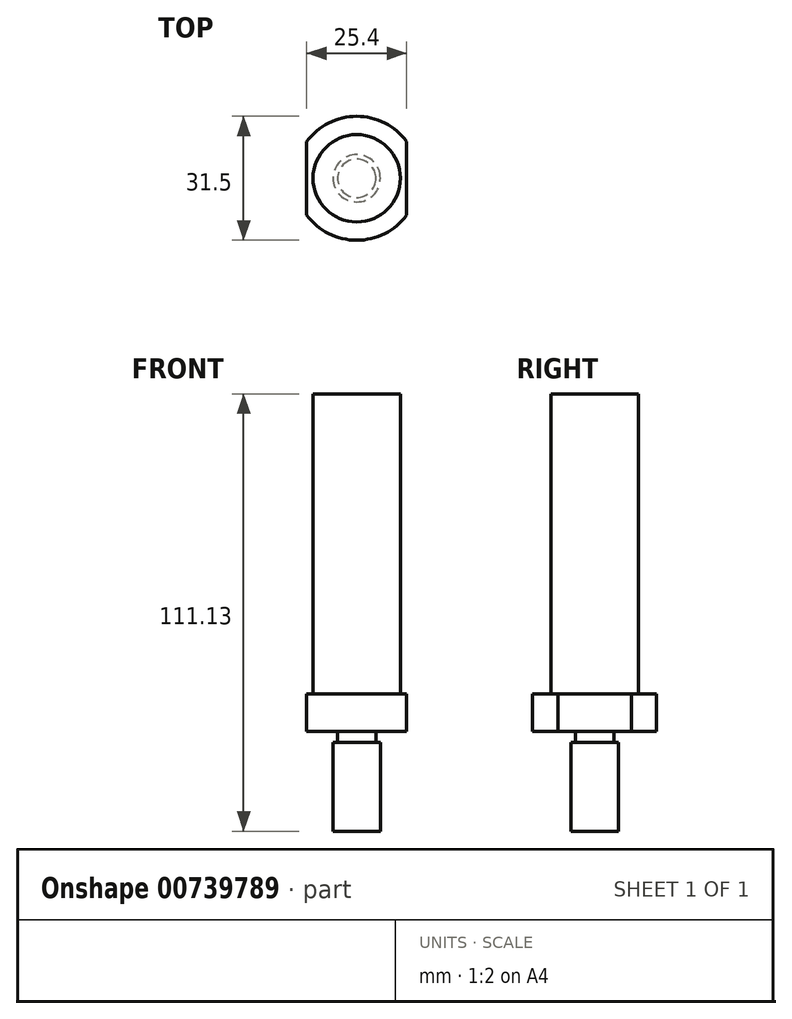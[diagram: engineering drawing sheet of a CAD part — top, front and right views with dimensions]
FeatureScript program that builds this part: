
annotation { "Feature Type Name" : "Feature", "Feature Type Description" : "" }
export const myFeature = defineFeature(function(context is Context, id is Id, definition is map)
    precondition{}
    {
        {
            var Q0;
            Q0=qCreatedBy(makeId("Top.planeOp"),FACE);
            var sketch = newSketch(context, id + "F0", { "sketchPlane" : qUnion([Q0])});
            skCircle(sketch, "E0", {"center": v(0, 0) * mm, "radius": 11.11 * mm});
            skSolve(sketch);
        }
        {
            var Q0;
            Q0 = qSketchRegion(id + "F0", true);
            extrude(context, id + "F1", {"entities" : qUnion([Q0]), "depth" : 76.2 * mm, "offsetDistance" : 25.4 * mm});
        }
        {
            var Q0;
            Q0=makeQuery(id+"F1.opExtrude","CAP_FACE",FACE,{"disambiguationData":[OSD([sQuery(id+"F0.wireOp",EDGE,"E0")])],"isStart":true});
            var sketch = newSketch(context, id + "F2", { "sketchPlane" : qUnion([Q0])});
            skCircle(sketch, "E1", {"center": v(0, 0) * mm, "radius": 15.75 * mm});
            skSolve(sketch);
        }
        {
            var Q0;
            Q0 = qSketchRegion(id + "F2", true);
            extrude(context, id + "F3", {"entities" : qUnion([Q0]), "operationType" : NewBodyOperationType.ADD, "depth" : 9.52 * mm, "offsetDistance" : 25.4 * mm});
        }
        {
            var Q0;
            Q0=makeQuery(id+"F3.opExtrude","CAP_FACE",FACE,{"disambiguationData":[OSD([sQuery(id+"F2.wireOp",EDGE,"E1")])],"isStart":false});
            var sketch = newSketch(context, id + "F4", { "sketchPlane" : qUnion([Q0])});
            skCircle(sketch, "E2", {"center": v(0, 0) * mm, "radius": 6 * mm});
            skSolve(sketch);
        }
        {
            var Q0;
            Q0 = qSketchRegion(id + "F4", true);
            extrude(context, id + "F5", {"entities" : qUnion([Q0]), "operationType" : NewBodyOperationType.ADD, "depth" : 25.4 * mm, "offsetDistance" : 25.4 * mm});
        }
        {
            var Q0;
            Q0=makeQuery(id+"F3.opExtrude","CAP_FACE",FACE,{"disambiguationData":[OSD([sQuery(id+"F2.wireOp",EDGE,"E1")])],"isStart":false});
            var sketch = newSketch(context, id + "F6", { "sketchPlane" : qUnion([Q0])});
            skCircle(sketch, "E3", {"center": v(0, 0) * mm, "radius": 4.89 * mm});
            skCircle(sketch, "E4.0", {"center": v(0, 0) * mm, "radius": 6 * mm});
            skSolve(sketch);
        }
        {
            var Q0;
            Q0 = qSketchRegion(id + "F6", true);
            extrude(context, id + "F7", {"entities" : qUnion([Q0]), "operationType" : NewBodyOperationType.REMOVE, "depth" : 2.8 * mm, "offsetDistance" : 25.4 * mm});
        }
        {
            var Q0;
            Q0=makeQuery(id+"F7.boolean.opBoolean","MERGE",FACE,{"derivedFrom":[makeQuery(id+"F3.opExtrude","CAP_FACE",FACE,{"disambiguationData":[OSD([sQuery(id+"F2.wireOp",EDGE,"E1")])],"isStart":false}),makeQuery(id+"F7.opExtrude","CAP_FACE",FACE,{"disambiguationData":[OSD([sQuery(id+"F6.wireOp",EDGE,"E3"),sQuery(id+"F6.wireOp",EDGE,"E4.0")])],"isStart":true})]});
            var sketch = newSketch(context, id + "F8", { "sketchPlane" : qUnion([Q0])});
            skLineSegment(sketch, "E5.left", {"start": v(-12.7, 24.53) * mm, "end": v(-12.7, -24.53) * mm});
            skLineSegment(sketch, "E5.right", {"start": v(12.7, 24.53) * mm, "end": v(12.7, -24.53) * mm});
            skPoint(sketch, "E5.middle", {"position": v(0, 0) * mm});
            skLineSegment(sketch, "E6.bottom", {"start": v(-12.7, 24.53) * mm, "end": v(-26.14, 24.53) * mm});
            skLineSegment(sketch, "E6.top", {"start": v(-12.7, -24.53) * mm, "end": v(-26.14, -24.53) * mm});
            skLineSegment(sketch, "E6.right", {"start": v(-26.14, 24.53) * mm, "end": v(-26.14, -24.53) * mm});
            skLineSegment(sketch, "E7", {"start": v(0, -24.53) * mm, "end": v(0, 24.53) * mm, "construction": true});
            skLineSegment(sketch, "E8.MirrorCS", {"start": v(12.7, 24.53) * mm, "end": v(26.14, 24.53) * mm});
            skLineSegment(sketch, "E9.MirrorCS", {"start": v(26.14, 24.53) * mm, "end": v(26.14, -24.53) * mm});
            skLineSegment(sketch, "E10.MirrorCS", {"start": v(12.7, -24.53) * mm, "end": v(26.14, -24.53) * mm});
            skSolve(sketch);
        }
        {
            var Q0;
            Q0 = qSketchRegion(id + "F8", true);
            extrude(context, id + "F9", {"entities" : qUnion([Q0]), "operationType" : NewBodyOperationType.REMOVE, "endBound" : BoundingType.THROUGH_ALL, "oppositeDirection" : true, "depth" : 25.4 * mm, "offsetDistance" : 25.4 * mm});
        }
    });
